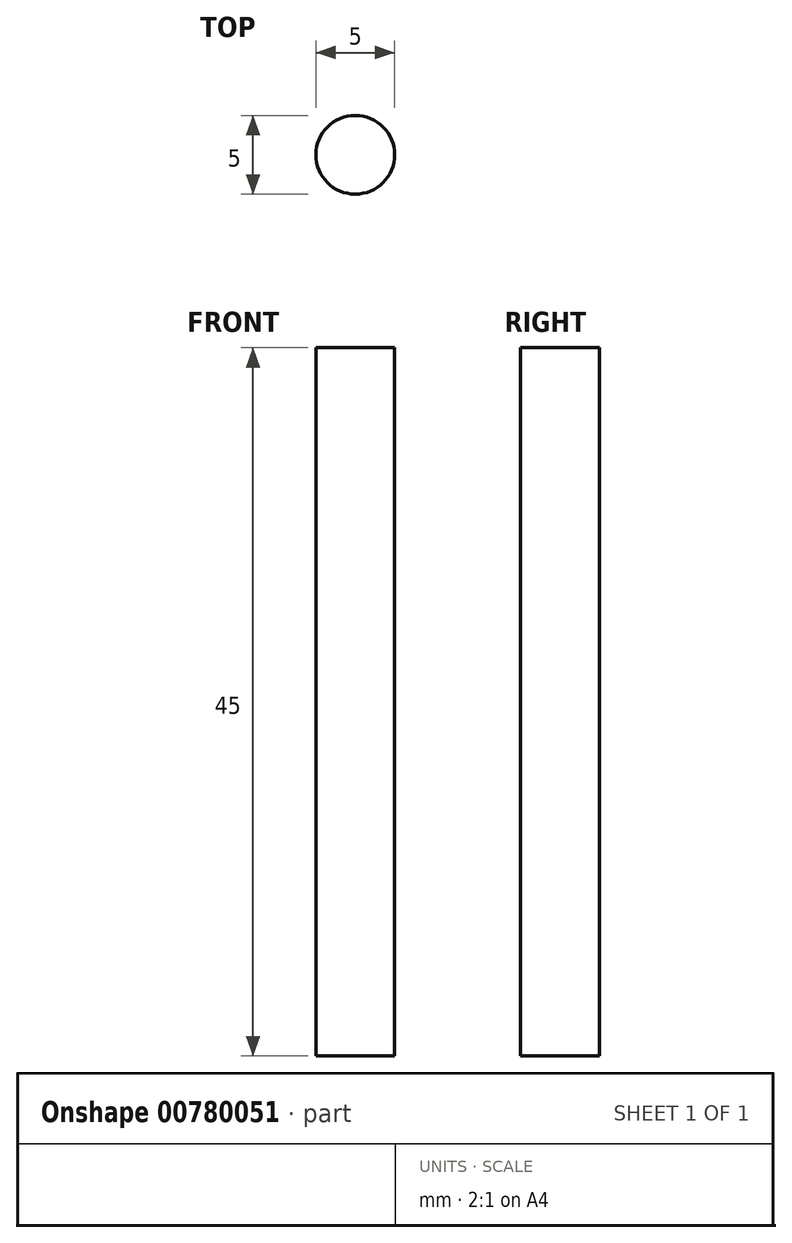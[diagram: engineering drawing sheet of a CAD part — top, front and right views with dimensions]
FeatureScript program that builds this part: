
annotation { "Feature Type Name" : "Feature", "Feature Type Description" : "" }
export const myFeature = defineFeature(function(context is Context, id is Id, definition is map)
    precondition{}
    {
        {
            var Q0;
            Q0=qCreatedBy(makeId("Top.planeOp"),FACE);
            var sketch = newSketch(context, id + "F0", { "sketchPlane" : qUnion([Q0])});
            skCircle(sketch, "E0", {"center": v(0, 0) * mm, "radius": 2.5 * mm});
            skSolve(sketch);
        }
        {
            var Q0;
            Q0=makeQuery(id+"F0.imprint","IMPRINT",FACE,{"disambiguationData":[TD([[makeQuery(id+"F0.imprint","IMPRINT",EDGE,{"derivedFrom":sQuery(id+"F0.wireOp",EDGE,"E0")}),1.0]])]});
            extrude(context, id + "F1", {"entities" : qUnion([Q0]), "depth" : 45 * mm, "offsetDistance" : 25 * mm});
        }
    });
